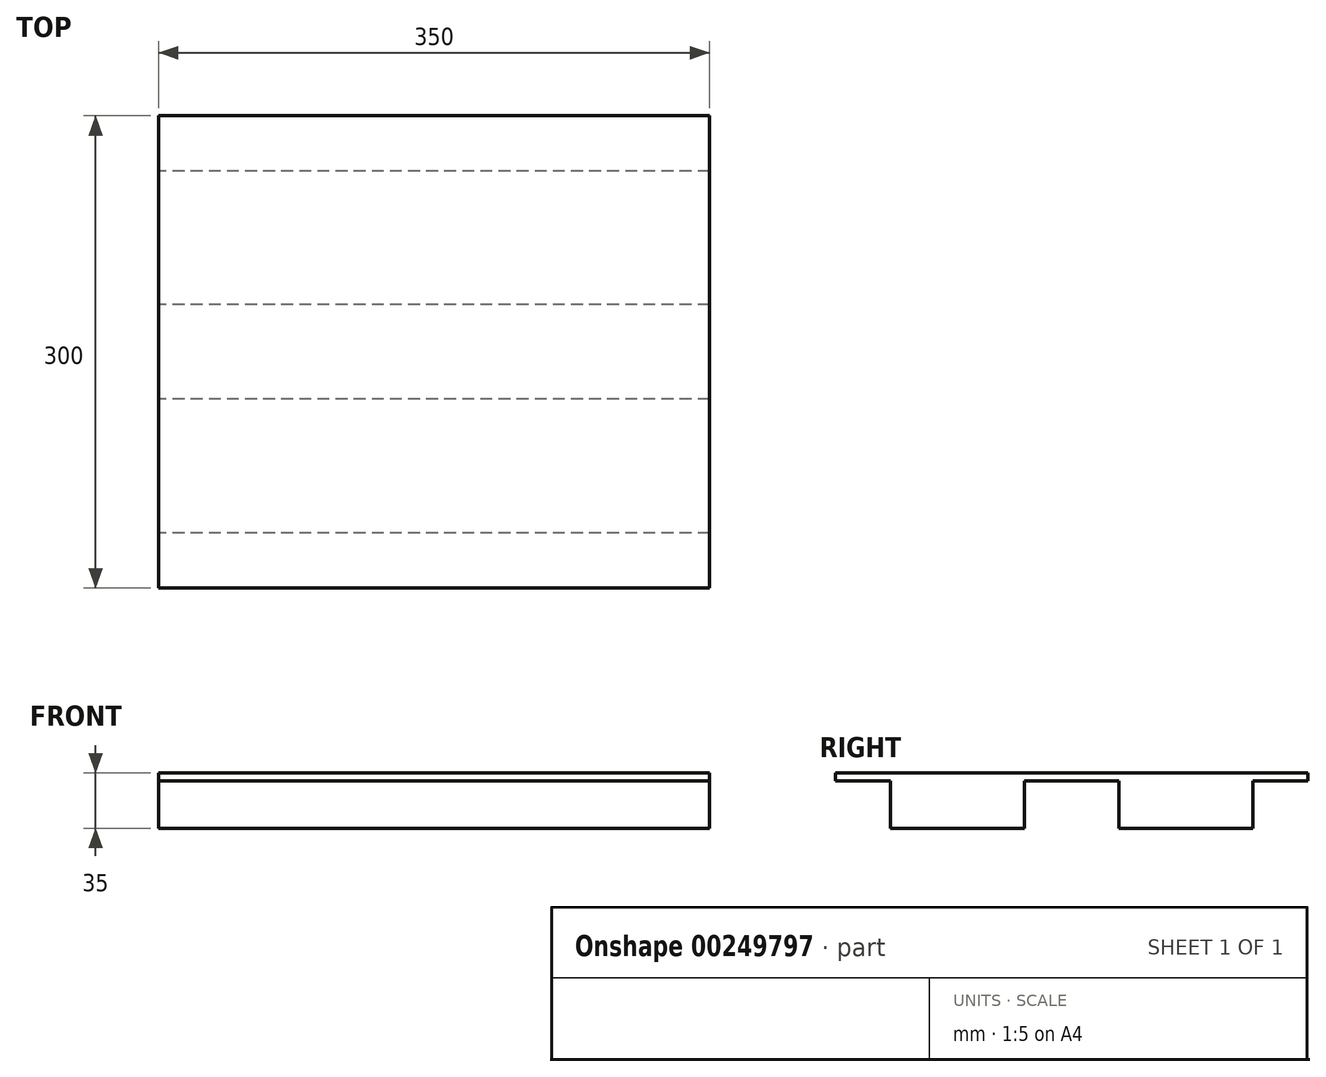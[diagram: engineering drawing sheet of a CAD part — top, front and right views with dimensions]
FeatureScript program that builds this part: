
annotation { "Feature Type Name" : "Feature", "Feature Type Description" : "" }
export const myFeature = defineFeature(function(context is Context, id is Id, definition is map)
    precondition{}
    {
        {
            var Q0;
            Q0=qCreatedBy(makeId("Top.planeOp"),FACE);
            var sketch = newSketch(context, id + "F0", { "sketchPlane" : qUnion([Q0])});
            skLineSegment(sketch, "E0.bottom", {"start": v(175, 150) * mm, "end": v(-175, 150) * mm});
            skLineSegment(sketch, "E0.top", {"start": v(175, -150) * mm, "end": v(-175, -150) * mm});
            skLineSegment(sketch, "E0.left", {"start": v(175, 150) * mm, "end": v(175, -150) * mm});
            skLineSegment(sketch, "E0.right", {"start": v(-175, 150) * mm, "end": v(-175, -150) * mm});
            skPoint(sketch, "E0.middle", {"position": v(0, 0) * mm});
            skSolve(sketch);
        }
        {
            var Q0;
            Q0=makeQuery(id+"F0.imprint","IMPRINT",FACE,{"disambiguationData":[TD([[makeQuery(id+"F0.imprint","IMPRINT",EDGE,{"derivedFrom":sQuery(id+"F0.wireOp",EDGE,"E0.bottom")}),1.0]])]});
            extrude(context, id + "F1", {"entities" : qUnion([Q0]), "depth" : 5 * mm});
        }
        {
            var Q0;
            Q0=makeQuery(id+"F1.opExtrude","CAP_FACE",FACE,{"disambiguationData":[OSD([sQuery(id+"F0.wireOp",EDGE,"E0.bottom"),sQuery(id+"F0.wireOp",EDGE,"E0.top"),sQuery(id+"F0.wireOp",EDGE,"E0.left"),sQuery(id+"F0.wireOp",EDGE,"E0.right")])],"isStart":true});
            var sketch = newSketch(context, id + "F2", { "sketchPlane" : qUnion([Q0])});
            skLineSegment(sketch, "E1.bottom", {"start": v(175, 115) * mm, "end": v(-175, 115) * mm});
            skLineSegment(sketch, "E1.top", {"start": v(175, -115) * mm, "end": v(-175, -115) * mm});
            skPoint(sketch, "E1.middle", {"position": v(0, 0) * mm});
            skLineSegment(sketch, "E2.bottom", {"start": v(175, 30) * mm, "end": v(-175, 30) * mm});
            skLineSegment(sketch, "E2.top", {"start": v(175, -30) * mm, "end": v(-175, -30) * mm});
            skLineSegment(sketch, "E3", {"start": v(-175, 115) * mm, "end": v(-175, 30) * mm});
            skLineSegment(sketch, "E4", {"start": v(-175, -30) * mm, "end": v(-175, -115) * mm});
            skLineSegment(sketch, "E5", {"start": v(175, 115) * mm, "end": v(175, 30) * mm});
            skLineSegment(sketch, "E6", {"start": v(175, -30) * mm, "end": v(175, -115) * mm});
            skSolve(sketch);
        }
        {
            var Q0;
            Q0 = qSketchRegion(id + "F2", true);
            extrude(context, id + "F3", {"entities" : qUnion([Q0]), "operationType" : NewBodyOperationType.ADD, "depth" : 30 * mm});
        }
    });
